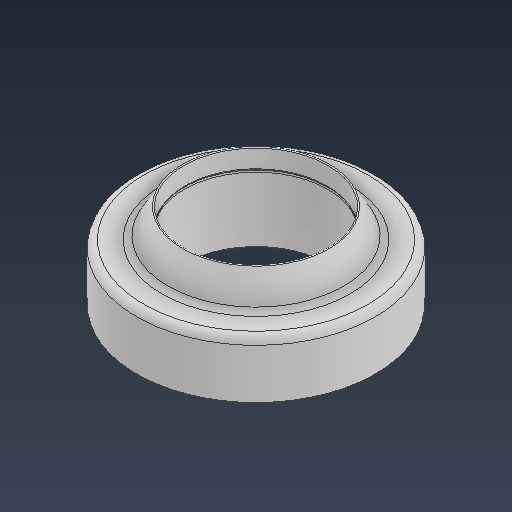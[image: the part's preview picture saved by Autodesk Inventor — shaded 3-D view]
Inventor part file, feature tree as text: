
AUTODESK INVENTOR PART (.ipt)
format: ipt  version: 2021 (Build 250183000, 183)  size: 208,896 bytes
history: native  units: in
note: dims shown in document units (in); Inventor stores cm internally (conversion verified against a paired STEP export)
features: revolve x1
ambient origin geometry x8: Origin, YZ Plane, XZ Plane, XY Plane, X Axis, Y Axis, Z Axis, Center Point
bodies: Solid1 (feature_tree)
feature tree (1):
  revolve  "Revolve1"  [1 undecoded]
note: 1 required parameter value undecoded (feature->parameter linkage not recoverable at this tier; creation-order binding heuristic only, values carry confidence <= 0.55)
